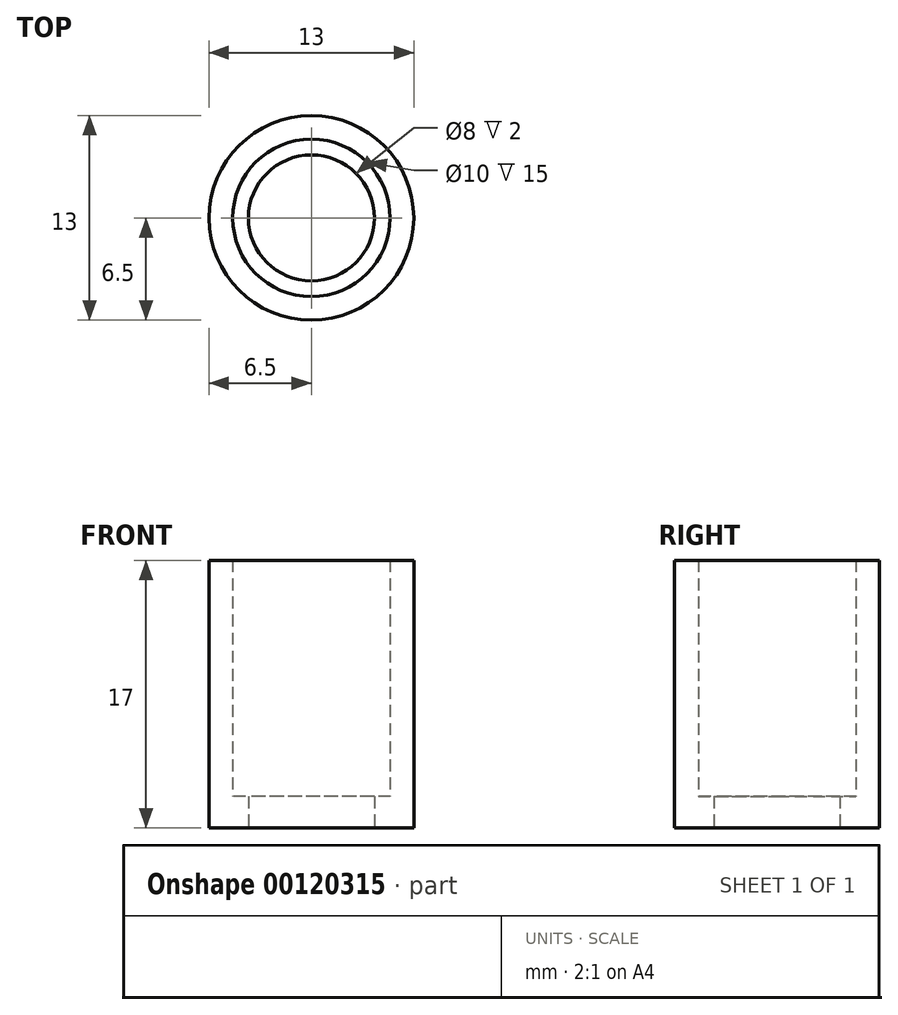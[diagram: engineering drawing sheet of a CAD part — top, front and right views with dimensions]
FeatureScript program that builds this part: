
annotation { "Feature Type Name" : "Feature", "Feature Type Description" : "" }
export const myFeature = defineFeature(function(context is Context, id is Id, definition is map)
    precondition{}
    {
        {
            var Q0;
            Q0=qCreatedBy(makeId("Top.planeOp"),FACE);
            var sketch = newSketch(context, id + "F0", { "sketchPlane" : qUnion([Q0])});
            skCircle(sketch, "E0", {"center": v(0, 0) * mm, "radius": 4 * mm});
            skCircle(sketch, "E1", {"center": v(0, 0) * mm, "radius": 6.5 * mm});
            skCircle(sketch, "E2", {"center": v(0, 0) * mm, "radius": 4.5 * mm, "construction": true});
            skCircle(sketch, "E3", {"center": v(0, 0) * mm, "radius": 5 * mm, "construction": true});
            skSolve(sketch);
        }
        {
            var Q0;
            Q0 = qSketchRegion(id + "F0", true);
            extrude(context, id + "F1", {"entities" : qUnion([Q0]), "depth" : 2 * mm});
        }
        {
            var Q0;
            Q0=makeQuery(id+"F1.opExtrude","CAP_FACE",FACE,{"disambiguationData":[OSD([sQuery(id+"F0.wireOp",EDGE,"E0"),sQuery(id+"F0.wireOp",EDGE,"E1")])],"isStart":false});
            var sketch = newSketch(context, id + "F2", { "sketchPlane" : qUnion([Q0])});
            skCircle(sketch, "E4", {"center": v(0, 0) * mm, "radius": 5 * mm});
            skCircle(sketch, "E5", {"center": v(0, 0) * mm, "radius": 6.5 * mm});
            skSolve(sketch);
        }
        {
            var Q0;
            Q0=makeQuery(id+"F2.imprint","IMPRINT",FACE,{"disambiguationData":[TD([[makeQuery(id+"F2.imprint","IMPRINT",EDGE,{"derivedFrom":sQuery(id+"F2.wireOp",EDGE,"E4")}),-1.0]])]});
            extrude(context, id + "F3", {"entities" : qUnion([Q0]), "operationType" : NewBodyOperationType.ADD, "depth" : 15 * mm});
        }
    });
